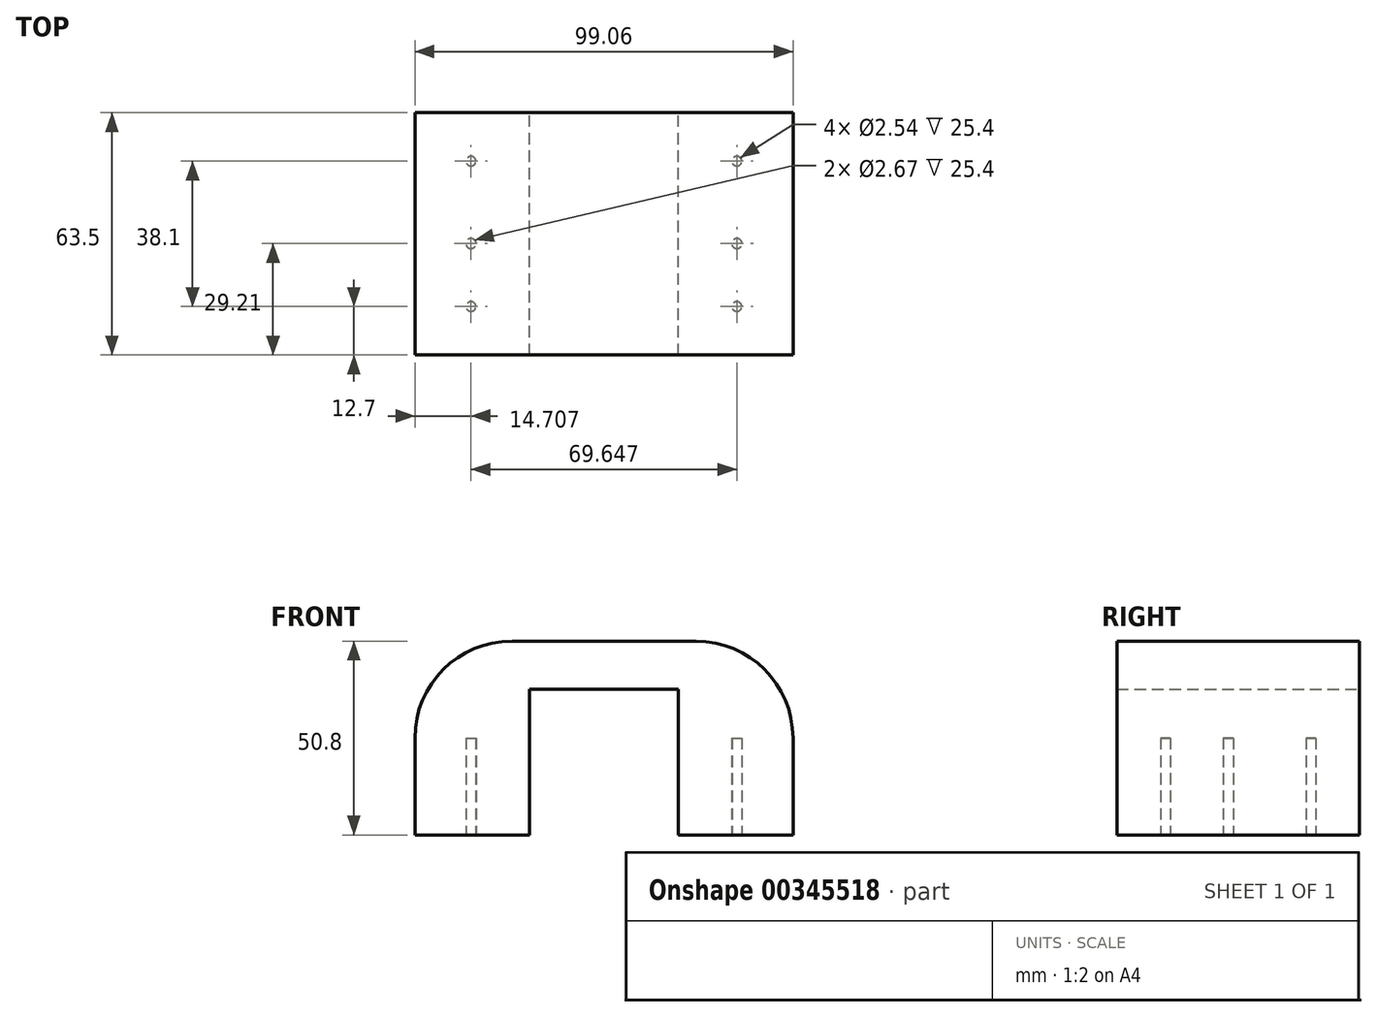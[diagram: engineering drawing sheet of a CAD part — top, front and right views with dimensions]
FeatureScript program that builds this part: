
annotation { "Feature Type Name" : "Feature", "Feature Type Description" : "" }
export const myFeature = defineFeature(function(context is Context, id is Id, definition is map)
    precondition{}
    {
        {
            var Q0;
            Q0=qCreatedBy(makeId("Front.planeOp"),FACE);
            var sketch = newSketch(context, id + "F0", { "sketchPlane" : qUnion([Q0])});
            skLineSegment(sketch, "E0", {"start": v(0, 0) * mm, "end": v(0, 50.8) * mm});
            skLineSegment(sketch, "E1", {"start": v(0, 50.8) * mm, "end": v(99.06, 50.8) * mm});
            skLineSegment(sketch, "E2", {"start": v(99.06, 50.8) * mm, "end": v(99.06, 0) * mm});
            skLineSegment(sketch, "E3", {"start": v(99.06, 0) * mm, "end": v(69.02, 0) * mm});
            skLineSegment(sketch, "E4", {"start": v(69.02, 0) * mm, "end": v(69.02, 38.18) * mm});
            skLineSegment(sketch, "E5", {"start": v(69.02, 38.18) * mm, "end": v(30.04, 38.18) * mm});
            skLineSegment(sketch, "E6", {"start": v(30.04, 38.18) * mm, "end": v(30.04, 0) * mm});
            skLineSegment(sketch, "E7", {"start": v(30.04, 0) * mm, "end": v(0, 0) * mm});
            skSolve(sketch);
        }
        {
            var Q0;
            Q0 = qSketchRegion(id + "F0", true);
            extrude(context, id + "F1", {"entities" : qUnion([Q0]), "depth" : 63.5 * mm});
        }
        {
            var Q0;
            Q0=makeQuery(id+"F1.opExtrude","SWEPT_EDGE",EDGE,{"disambiguationData":[OSD([sQuery(id+"F0.wireOp",EDGE,"E1"),sQuery(id+"F0.wireOp",EDGE,"E2")])]});
            var Q1;
            Q1=makeQuery(id+"F1.opExtrude","SWEPT_EDGE",EDGE,{"disambiguationData":[OSD([sQuery(id+"F0.wireOp",EDGE,"E0"),sQuery(id+"F0.wireOp",EDGE,"E1")])]});
            fillet(context, id + "F2", {"entities" : qUnion([Q0, Q1]), "radius" : 25.4 * mm, "tangentPropagation" : true, "allowEdgeOverflow" : false});
        }
        {
            var Q0;
            Q0=makeQuery(id+"F1.opExtrude","SWEPT_FACE",FACE,{"disambiguationData":[OSD([sQuery(id+"F0.wireOp",EDGE,"E3")])]});
            var sketch = newSketch(context, id + "F3", { "sketchPlane" : qUnion([Q0])});
            skCircle(sketch, "E8", {"center": v(14.7, 34.3) * mm, "radius": 1.33 * mm});
            skCircle(sketch, "E9", {"center": v(84.35, 34.3) * mm, "radius": 1.33 * mm});
            skCircle(sketch, "E10", {"center": v(14.7, 12.7) * mm, "radius": 1.27 * mm});
            skCircle(sketch, "E11", {"center": v(84.35, 12.7) * mm, "radius": 1.27 * mm});
            skCircle(sketch, "E12", {"center": v(84.35, 50.8) * mm, "radius": 1.27 * mm});
            skCircle(sketch, "E13", {"center": v(14.7, 50.8) * mm, "radius": 1.27 * mm});
            skSolve(sketch);
        }
        {
            var Q0;
            Q0 = qSketchRegion(id + "F3", true);
            extrude(context, id + "F4", {"entities" : qUnion([Q0]), "operationType" : NewBodyOperationType.REMOVE, "oppositeDirection" : true, "depth" : 25.4 * mm});
        }
    });
